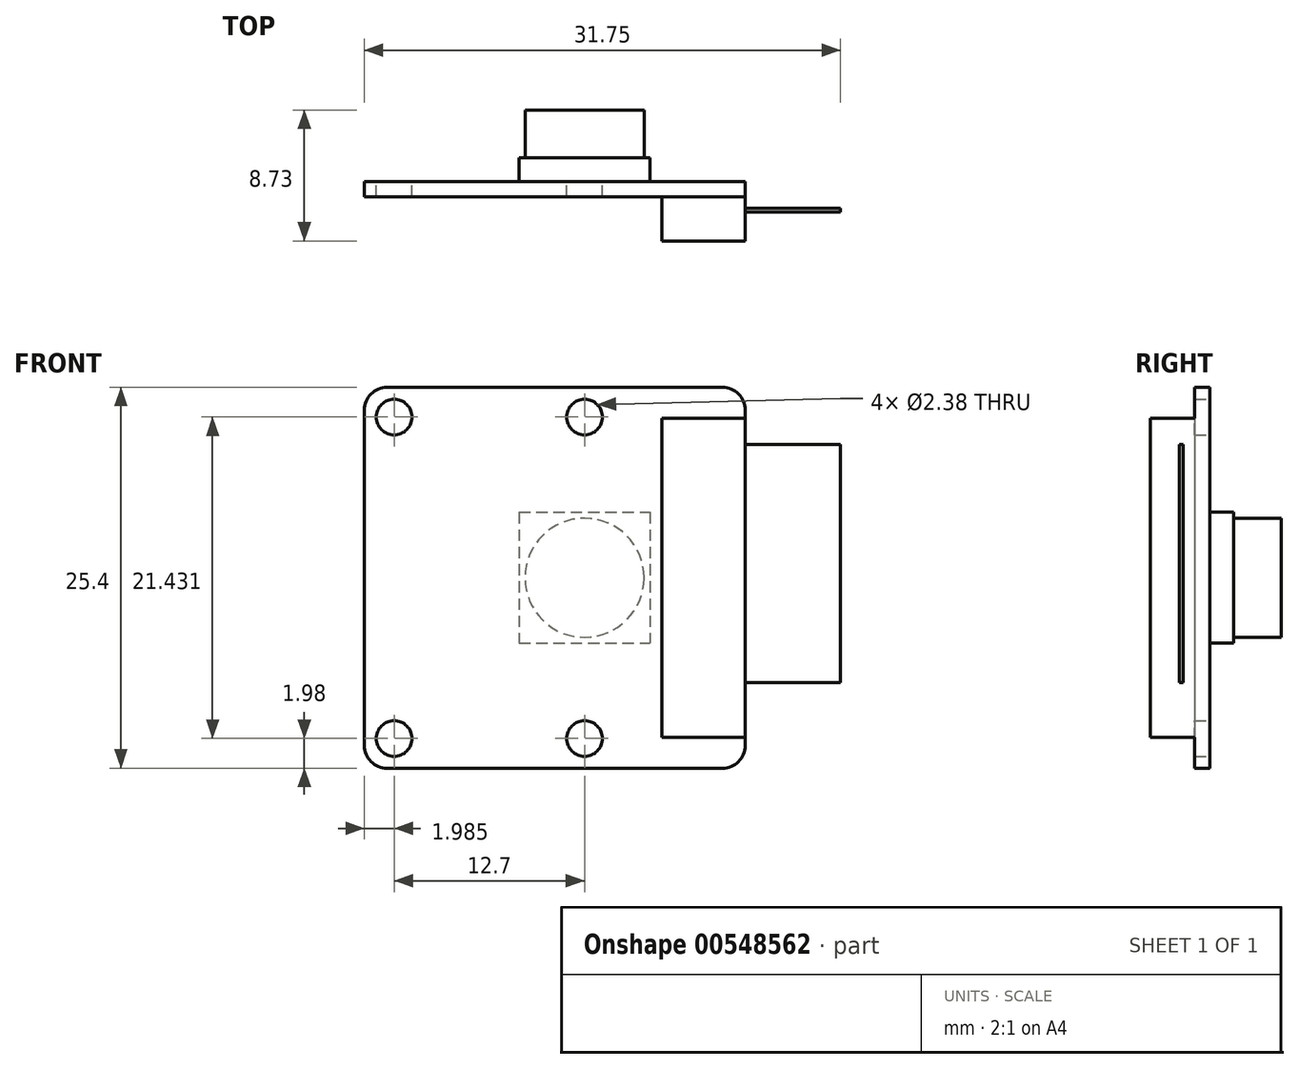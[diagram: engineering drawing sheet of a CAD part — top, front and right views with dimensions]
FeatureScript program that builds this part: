
annotation { "Feature Type Name" : "Feature", "Feature Type Description" : "" }
export const myFeature = defineFeature(function(context is Context, id is Id, definition is map)
    precondition{}
    {
        {
            var Q0;
            Q0=qCreatedBy(makeId("Front.planeOp"),FACE);
            var sketch = newSketch(context, id + "F0", { "sketchPlane" : qUnion([Q0])});
            skLineSegment(sketch, "E0.bottom", {"start": v(13.54, 11.75) * mm, "end": v(-11.86, 11.75) * mm});
            skLineSegment(sketch, "E0.top", {"start": v(13.54, -13.65) * mm, "end": v(-11.86, -13.65) * mm});
            skLineSegment(sketch, "E0.left", {"start": v(13.54, 11.75) * mm, "end": v(13.54, -13.65) * mm});
            skLineSegment(sketch, "E0.right", {"start": v(-11.86, 11.75) * mm, "end": v(-11.86, -13.65) * mm});
            skLineSegment(sketch, "E1", {"start": v(-9.88, 11.75) * mm, "end": v(-9.88, -13.65) * mm, "construction": true});
            skLineSegment(sketch, "E2", {"start": v(-11.86, -0.95) * mm, "end": v(13.54, -0.95) * mm, "construction": true});
            skCircle(sketch, "E3", {"center": v(-9.88, 9.76) * mm, "radius": 1.2 * mm});
            skCircle(sketch, "E4", {"center": v(-9.88, -11.67) * mm, "radius": 1.2 * mm});
            skLineSegment(sketch, "E5", {"start": v(2.82, 11.75) * mm, "end": v(2.82, -13.65) * mm, "construction": true});
            skCircle(sketch, "E6", {"center": v(2.82, 9.76) * mm, "radius": 1.2 * mm});
            skCircle(sketch, "E7", {"center": v(2.82, -11.67) * mm, "radius": 1.2 * mm});
            skCircle(sketch, "E8", {"center": v(2.82, -0.95) * mm, "radius": 3.97 * mm});
            skLineSegment(sketch, "E9.bottom", {"start": v(-1.54, 3.41) * mm, "end": v(7.2, 3.41) * mm});
            skLineSegment(sketch, "E9.top", {"start": v(-1.54, -5.32) * mm, "end": v(7.2, -5.32) * mm});
            skLineSegment(sketch, "E9.left", {"start": v(-1.54, 3.41) * mm, "end": v(-1.54, -5.32) * mm});
            skLineSegment(sketch, "E9.right", {"start": v(7.2, 3.41) * mm, "end": v(7.2, -5.32) * mm});
            skCircle(sketch, "E10", {"center": v(2.82, 15.28) * mm, "radius": 1.5 * mm});
            skSolve(sketch);
        }
        {
            var Q0;
            Q0=makeQuery(id+"F0.imprint","IMPRINT",FACE,{"disambiguationData":[TD([[makeQuery(id+"F0.imprint","IMPRINT",EDGE,{"derivedFrom":sQuery(id+"F0.wireOp",EDGE,"E0.bottom")}),1.0]])]});
            var Q1;
            Q1=makeQuery(id+"F0.imprint","IMPRINT",FACE,{"disambiguationData":[TD([[makeQuery(id+"F0.imprint","IMPRINT",EDGE,{"derivedFrom":sQuery(id+"F0.wireOp",EDGE,"E8")}),-1.0]])]});
            var Q2;
            Q2=makeQuery(id+"F0.imprint","IMPRINT",FACE,{"disambiguationData":[TD([[makeQuery(id+"F0.imprint","IMPRINT",EDGE,{"derivedFrom":sQuery(id+"F0.wireOp",EDGE,"E8")}),1.0]])]});
            extrude(context, id + "F1", {"entities" : qUnion([Q0, Q1, Q2]), "depth" : 1.02 * mm});
        }
        {
            var Q0;
            Q0=makeQuery(id+"F0.imprint","IMPRINT",FACE,{"disambiguationData":[TD([[makeQuery(id+"F0.imprint","IMPRINT",EDGE,{"derivedFrom":sQuery(id+"F0.wireOp",EDGE,"E8")}),-1.0]])]});
            var Q1;
            Q1=makeQuery(id+"F0.imprint","IMPRINT",FACE,{"disambiguationData":[TD([[makeQuery(id+"F0.imprint","IMPRINT",EDGE,{"derivedFrom":sQuery(id+"F0.wireOp",EDGE,"E8")}),1.0]])]});
            extrude(context, id + "F2", {"entities" : qUnion([Q0, Q1]), "operationType" : NewBodyOperationType.ADD, "oppositeDirection" : true, "depth" : 1.59 * mm});
        }
        {
            var Q0;
            Q0=makeQuery(id+"F0.imprint","IMPRINT",FACE,{"disambiguationData":[TD([[makeQuery(id+"F0.imprint","IMPRINT",EDGE,{"derivedFrom":sQuery(id+"F0.wireOp",EDGE,"E8")}),1.0]])]});
            extrude(context, id + "F3", {"entities" : qUnion([Q0]), "operationType" : NewBodyOperationType.ADD, "oppositeDirection" : true, "depth" : 4.76 * mm});
        }
        {
            var Q0;
            Q0=makeQuery(id+"F1.opExtrude","SWEPT_EDGE",EDGE,{"disambiguationData":[OSD([sQuery(id+"F0.wireOp",EDGE,"E0.bottom"),sQuery(id+"F0.wireOp",EDGE,"E0.right")])]});
            var Q1;
            Q1=makeQuery(id+"F1.opExtrude","SWEPT_EDGE",EDGE,{"disambiguationData":[OSD([sQuery(id+"F0.wireOp",EDGE,"E0.top"),sQuery(id+"F0.wireOp",EDGE,"E0.right")])]});
            var Q2;
            Q2=makeQuery(id+"F1.opExtrude","SWEPT_EDGE",EDGE,{"disambiguationData":[OSD([sQuery(id+"F0.wireOp",EDGE,"E0.top"),sQuery(id+"F0.wireOp",EDGE,"E0.left")])]});
            var Q3;
            Q3=makeQuery(id+"F1.opExtrude","SWEPT_EDGE",EDGE,{"disambiguationData":[OSD([sQuery(id+"F0.wireOp",EDGE,"E0.bottom"),sQuery(id+"F0.wireOp",EDGE,"E0.left")])]});
            fillet(context, id + "F4", {"entities" : qUnion([Q0, Q1, Q2, Q3]), "radius" : 1.52 * mm, "tangentPropagation" : true, "allowEdgeOverflow" : false});
        }
        {
            var Q0;
            Q0=makeQuery(id+"F1.opExtrude","CAP_FACE",FACE,{"disambiguationData":[OSD([sQuery(id+"F0.wireOp",EDGE,"E0.bottom"),sQuery(id+"F0.wireOp",EDGE,"E0.top"),sQuery(id+"F0.wireOp",EDGE,"E0.left"),sQuery(id+"F0.wireOp",EDGE,"E0.right"),sQuery(id+"F0.wireOp",EDGE,"E3"),sQuery(id+"F0.wireOp",EDGE,"E4"),sQuery(id+"F0.wireOp",EDGE,"E6"),sQuery(id+"F0.wireOp",EDGE,"E7")])],"isStart":false});
            var sketch = newSketch(context, id + "F5", { "sketchPlane" : qUnion([Q0])});
            skLineSegment(sketch, "E11.bottom", {"start": v(7.98, 9.69) * mm, "end": v(13.54, 9.69) * mm});
            skLineSegment(sketch, "E11.top", {"start": v(7.98, -11.6) * mm, "end": v(13.54, -11.6) * mm});
            skLineSegment(sketch, "E11.left", {"start": v(7.98, 9.69) * mm, "end": v(7.98, -11.6) * mm});
            skLineSegment(sketch, "E11.right", {"start": v(13.54, 9.69) * mm, "end": v(13.54, -11.6) * mm});
            skLineSegment(sketch, "E12", {"start": v(-11.86, -0.95) * mm, "end": v(42.66, -0.95) * mm, "construction": true});
            skPoint(sketch, "E12.endSnap0", {"position": v(-11.86, -0.95) * mm});
            skSolve(sketch);
        }
        {
            var Q0;
            Q0=qSketchRegion(id+"F5",true);
            extrude(context, id + "F6", {"entities" : qUnion([Q0]), "operationType" : NewBodyOperationType.ADD, "depth" : 2.95 * mm});
        }
        {
            var Q0;
            Q0=makeQuery(id+"F6.boolean.opBoolean","MERGE",FACE,{"derivedFrom":[makeQuery(id+"F1.opExtrude","SWEPT_FACE",FACE,{"disambiguationData":[OSD([sQuery(id+"F0.wireOp",EDGE,"E0.left")])]}),makeQuery(id+"F6.opExtrude","SWEPT_FACE",FACE,{"disambiguationData":[OSD([sQuery(id+"F5.wireOp",EDGE,"E11.right")])]})]});
            var sketch = newSketch(context, id + "F7", { "sketchPlane" : qUnion([Q0])});
            skLineSegment(sketch, "E13", {"start": v(0, 0) * mm, "end": v(-13.8, 0) * mm, "construction": true});
            skLineSegment(sketch, "E14.bottom", {"start": v(-2.03, 7.94) * mm, "end": v(-1.78, 7.94) * mm});
            skLineSegment(sketch, "E14.top", {"start": v(-2.03, -7.94) * mm, "end": v(-1.78, -7.94) * mm});
            skLineSegment(sketch, "E14.left", {"start": v(-2.03, 7.94) * mm, "end": v(-2.03, -7.94) * mm});
            skLineSegment(sketch, "E14.right", {"start": v(-1.78, 7.94) * mm, "end": v(-1.78, -7.94) * mm});
            skSolve(sketch);
        }
        {
            var Q0;
            Q0=qSketchRegion(id+"F7",true);
            extrude(context, id + "F8", {"entities" : qUnion([Q0]), "operationType" : NewBodyOperationType.ADD, "depth" : 6.35 * mm});
        }
    });
